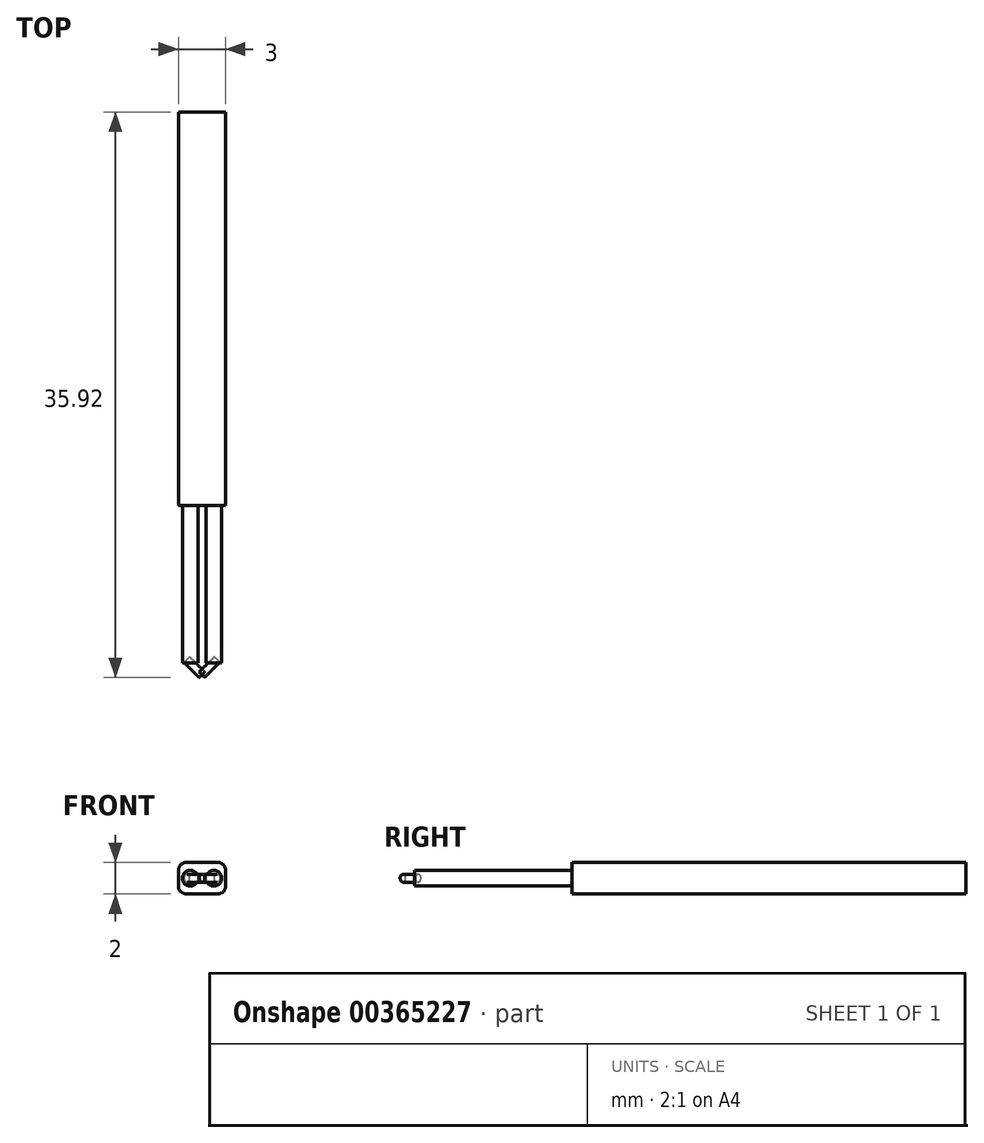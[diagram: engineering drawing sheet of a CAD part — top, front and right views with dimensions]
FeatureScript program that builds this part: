
annotation { "Feature Type Name" : "Feature", "Feature Type Description" : "" }
export const myFeature = defineFeature(function(context is Context, id is Id, definition is map)
    precondition{}
    {
        {
            var Q0;
            Q0=qCreatedBy(makeId("Front.planeOp"),FACE);
            var sketch = newSketch(context, id + "F0", { "sketchPlane" : qUnion([Q0])});
            skLineSegment(sketch, "E0.bottom", {"start": v(1, -1) * mm, "end": v(-1, -1) * mm});
            skLineSegment(sketch, "E0.top", {"start": v(1, 1) * mm, "end": v(-1, 1) * mm});
            skLineSegment(sketch, "E0.left", {"start": v(1.5, -0.5) * mm, "end": v(1.5, 0.5) * mm});
            skLineSegment(sketch, "E0.right", {"start": v(-1.5, -0.5) * mm, "end": v(-1.5, 0.5) * mm});
            skPoint(sketch, "E0.middle", {"position": v(0, 0) * mm});
            skPoint(sketch, "E1.visualSharp", {"position": v(-1.5, 1) * mm});
            skArc(sketch, "E1.filletArc", {"start": v(-1, 1) * mm, "mid": v(-1.35, 0.85) * mm, "end": v(-1.5, 0.5) * mm});
            skPoint(sketch, "E2.visualSharp", {"position": v(1.5, 1) * mm});
            skArc(sketch, "E2.filletArc", {"start": v(1.5, 0.5) * mm, "mid": v(1.35, 0.85) * mm, "end": v(1, 1) * mm});
            skPoint(sketch, "E3.visualSharp", {"position": v(-1.5, -1) * mm});
            skArc(sketch, "E3.filletArc", {"start": v(-1.5, -0.5) * mm, "mid": v(-1.35, -0.85) * mm, "end": v(-1, -1) * mm});
            skPoint(sketch, "E4.visualSharp", {"position": v(1.5, -1) * mm});
            skArc(sketch, "E4.filletArc", {"start": v(1, -1) * mm, "mid": v(1.35, -0.85) * mm, "end": v(1.5, -0.5) * mm});
            skSolve(sketch);
        }
        {
            var Q0;
            Q0=makeQuery(id+"F0.imprint","IMPRINT",FACE,{"disambiguationData":[TD([[makeQuery(id+"F0.imprint","IMPRINT",EDGE,{"derivedFrom":sQuery(id+"F0.wireOp",EDGE,"E0.bottom")}),-1.0]])]});
            extrude(context, id + "F1", {"entities" : qUnion([Q0]), "depth" : 25 * mm});
        }
        {
            var Q0;
            Q0=makeQuery(id+"F1.opExtrude","CAP_FACE",FACE,{"disambiguationData":[OSD([sQuery(id+"F0.wireOp",EDGE,"E0.bottom"),sQuery(id+"F0.wireOp",EDGE,"E0.top"),sQuery(id+"F0.wireOp",EDGE,"E0.left"),sQuery(id+"F0.wireOp",EDGE,"E0.right"),sQuery(id+"F0.wireOp",EDGE,"E1.filletArc"),sQuery(id+"F0.wireOp",EDGE,"E2.filletArc"),sQuery(id+"F0.wireOp",EDGE,"E3.filletArc"),sQuery(id+"F0.wireOp",EDGE,"E4.filletArc")])],"isStart":false});
            var sketch = newSketch(context, id + "F2", { "sketchPlane" : qUnion([Q0])});
            skLineSegment(sketch, "E5", {"start": v(0, 0) * mm, "end": v(-1.5, 0) * mm, "construction": true});
            skLineSegment(sketch, "E6", {"start": v(0, 0) * mm, "end": v(1.5, 0) * mm, "construction": true});
            skCircle(sketch, "E7", {"center": v(-0.75, 0) * mm, "radius": 0.5 * mm});
            skCircle(sketch, "E8", {"center": v(0.75, 0) * mm, "radius": 0.5 * mm});
            skSolve(sketch);
        }
        {
            var Q0;
            Q0 = qSketchRegion(id + "F2", true);
            extrude(context, id + "F3", {"entities" : qUnion([Q0]), "depth" : 10 * mm});
        }
        {
            var Q0;
            Q0=qCreatedBy(makeId("Top.planeOp"),FACE);
            var sketch = newSketch(context, id + "F4", { "sketchPlane" : qUnion([Q0])});
            skLineSegment(sketch, "E9.0", {"start": v(-0.25, -35) * mm, "end": v(-1.25, -35) * mm, "construction": true});
            skLineSegment(sketch, "E10.0", {"start": v(1.25, -35) * mm, "end": v(0.25, -35) * mm, "construction": true});
            skLineSegment(sketch, "E11", {"start": v(-0.75, -35) * mm, "end": v(0, -35.75) * mm});
            skLineSegment(sketch, "E12", {"start": v(0, -35.75) * mm, "end": v(0.75, -35) * mm});
            skLineSegment(sketch, "E13", {"start": v(0.75, -35) * mm, "end": v(1.25, -35.5) * mm});
            skSolve(sketch);
        }
        {
            var Q0;
            Q0=sQuery(id+"F4.wireOp",EDGE,"E13");
            cPlane(context, id + "F5", {"entities" : qUnion([Q0]), "cplaneType" : CPlaneType.LINE_ANGLE, "offset" : 25 * mm, "angle" : 90 * degree, "width" : 150 * mm, "height" : 150 * mm});
        }
        {
            var Q0;
            Q0=qCreatedBy(id+"F5.planeOp",FACE);
            var sketch = newSketch(context, id + "F6", { "sketchPlane" : qUnion([Q0])});
            skCircle(sketch, "E14", {"center": v(-25.27, 0) * mm, "radius": 0.25 * mm});
            skSolve(sketch);
        }
        {
            var Q0;
            Q0 = qSketchRegion(id + "F6", true);
            var Q1;
            Q1=sQuery(id+"F4.wireOp",VERTEX,"E12.start");
            extrude(context, id + "F7", {"entities" : qUnion([Q0]), "depth" : .3 * mm, "hasSecondDirection" : true, "secondDirectionBound" : BoundingType.UP_TO_VERTEX, "secondDirectionOppositeDirection" : true, "secondDirectionBoundEntityVertex" : qUnion([Q1]), "secondDirectionDepth" : 25 * mm});
        }
        {
            var Q0;
            Q0=makeQuery(id+"F7.opExtrude","SWEPT_BODY",BODY,{"disambiguationData":[OSD([sQuery(id+"F6.wireOp",EDGE,"E14")])]});
            var Q1;
            Q1=qCreatedBy(makeId("Right.planeOp"),FACE);
            mirror(context, id + "F8", {"entities" : qUnion([Q0]), "mirrorPlane" : qUnion([Q1])});
        }
        {
            var Q0;
            Q0=qCreatedBy(makeId("Top.planeOp"),FACE);
            var sketch = newSketch(context, id + "F9", { "sketchPlane" : qUnion([Q0])});
            skLineSegment(sketch, "E15", {"start": v(1.14, -34.96) * mm, "end": v(0.17, -35.92) * mm, "construction": true});
            skLineSegment(sketch, "E16", {"start": v(-0.17, -35.92) * mm, "end": v(-1.14, -34.96) * mm, "construction": true});
            skLineSegment(sketch, "E17.0", {"start": v(0.96, -34.78) * mm, "end": v(0, -35.75) * mm, "construction": true});
            skLineSegment(sketch, "E18.0", {"start": v(0, -35.75) * mm, "end": v(-0.96, -34.78) * mm, "construction": true});
            skPoint(sketch, "E19", {"position": v(0, -35.74) * mm});
            skArc(sketch, "E20", {"start": v(0.3, -35.74) * mm, "mid": v(0, -35.44) * mm, "end": v(-0.3, -35.75) * mm});
            skSolve(sketch);
        }
        {
            var Q0;
            Q0=qCreatedBy(makeId("Top.planeOp"),FACE);
            var sketch = newSketch(context, id + "F10", { "sketchPlane" : qUnion([Q0])});
            skPoint(sketch, "E21.0", {"position": v(0.3, -35.74) * mm});
            skPoint(sketch, "E22.0", {"position": v(-0.3, -35.75) * mm});
            skLineSegment(sketch, "E23", {"start": v(-0.3, -35.75) * mm, "end": v(0.3, -35.74) * mm});
            skSolve(sketch);
        }
        {
            var Q0;
            Q0 = qSketchRegion(id + "F9", true);
            var Q1;
            Q1 = qConstructionFilter(qBodyType(qCreatedBy(id + "F9" ,EDGE), BodyType.WIRE), ConstructionObject.NO);
            var Q2;
            Q2=sQuery(id+"F10.wireOp",EDGE,"E23");
            revolve(context, id + "F11", {"bodyType" : ToolBodyType.SURFACE, "entities" : qUnion([Q0]), "surfaceEntities" : qUnion([Q1]), "axis" : qUnion([Q2]), "revolveType" : RevolveType.FULL});
        }
    });
